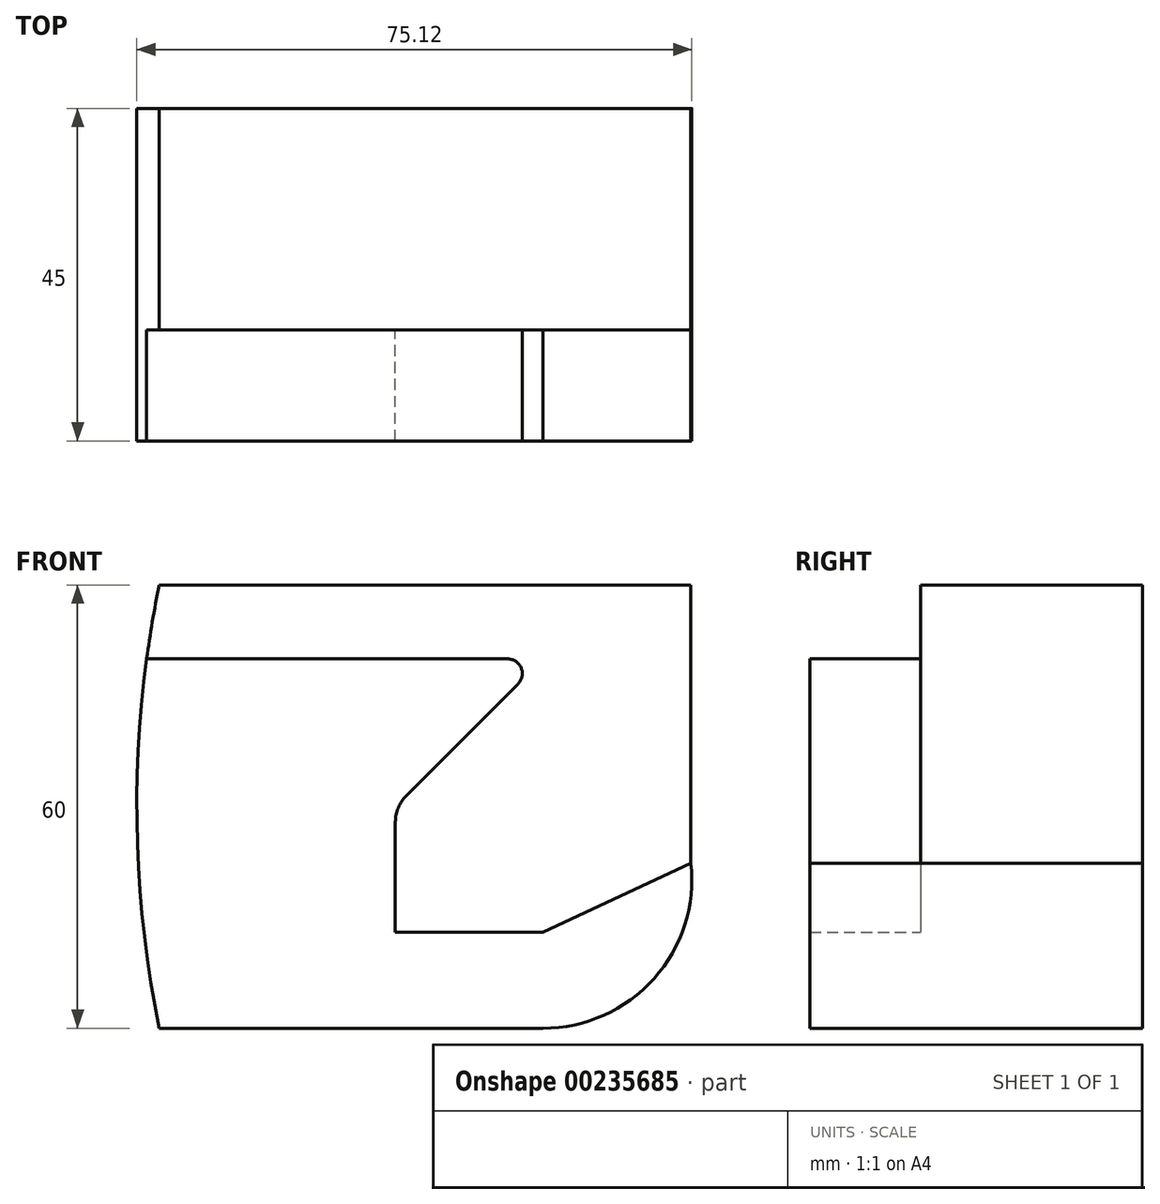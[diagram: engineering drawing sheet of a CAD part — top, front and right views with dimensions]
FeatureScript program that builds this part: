
annotation { "Feature Type Name" : "Feature", "Feature Type Description" : "" }
export const myFeature = defineFeature(function(context is Context, id is Id, definition is map)
    precondition{}
    {
        {
            var Q0;
            Q0=qCreatedBy(makeId("Front.planeOp"),FACE);
            var sketch = newSketch(context, id + "F0", { "sketchPlane" : qUnion([Q0])});
            skLineSegment(sketch, "E0", {"start": v(0, 0) * mm, "end": v(-51.97, 0) * mm});
            skLineSegment(sketch, "E1", {"start": v(-51.97, 60) * mm, "end": v(0, 60) * mm});
            skLineSegment(sketch, "E2", {"start": v(0, 60) * mm, "end": v(0, 50) * mm});
            skLineSegment(sketch, "E3", {"start": v(0, 50) * mm, "end": v(-18.54, 31.46) * mm});
            skLineSegment(sketch, "E4", {"start": v(-20, 27.93) * mm, "end": v(-20, 13) * mm});
            skLineSegment(sketch, "E5", {"start": v(-20, 13) * mm, "end": v(0, 13) * mm});
            skLineSegment(sketch, "E6", {"start": v(0, 13) * mm, "end": v(0, 0) * mm, "construction": true});
            skPoint(sketch, "E7.visualSharp", {"position": v(-20, 30) * mm});
            skArc(sketch, "E7.filletArc", {"start": v(-18.54, 31.46) * mm, "mid": v(-19.62, 29.84) * mm, "end": v(-20, 27.93) * mm});
            skArc(sketch, "E8", {"start": v(-51.97, 60) * mm, "mid": v(-55, 30) * mm, "end": v(-51.97, 0) * mm});
            skLineSegment(sketch, "E9", {"start": v(-51.97, 60) * mm, "end": v(-51.97, 0) * mm, "construction": true});
            skPoint(sketch, "E10", {"position": v(-51.97, 0) * mm});
            skArc(sketch, "E11", {"start": v(0, 0) * mm, "mid": v(14.99, 6.7) * mm, "end": v(20, 22.33) * mm});
            skLineSegment(sketch, "E12", {"start": v(20, 22.33) * mm, "end": v(0, 13) * mm});
            skSolve(sketch);
        }
        {
            var Q0;
            Q0 = qSketchRegion(id + "F0", true);
            extrude(context, id + "F1", {"entities" : qUnion([Q0]), "depth" : 30 * mm});
        }
        {
            var Q0;
            Q0=makeQuery(id+"F1.opExtrude","CAP_FACE",FACE,{"disambiguationData":[OSD([sQuery(id+"F0.wireOp",EDGE,"E0"),sQuery(id+"F0.wireOp",EDGE,"E1"),sQuery(id+"F0.wireOp",EDGE,"E2"),sQuery(id+"F0.wireOp",EDGE,"E3"),sQuery(id+"F0.wireOp",EDGE,"E4"),sQuery(id+"F0.wireOp",EDGE,"E5"),sQuery(id+"F0.wireOp",EDGE,"E7.filletArc"),sQuery(id+"F0.wireOp",EDGE,"E8"),sQuery(id+"F0.wireOp",EDGE,"E11"),sQuery(id+"F0.wireOp",EDGE,"E12")])],"isStart":true});
            var sketch = newSketch(context, id + "F2", { "sketchPlane" : qUnion([Q0])});
            skLineSegment(sketch, "E13.0", {"start": v(0, 60) * mm, "end": v(0, 50) * mm});
            skLineSegment(sketch, "E13.1", {"start": v(0, 50) * mm, "end": v(18.54, 31.46) * mm});
            skArc(sketch, "E13.2", {"start": v(18.54, 31.46) * mm, "mid": v(19.62, 29.84) * mm, "end": v(20, 27.93) * mm});
            skLineSegment(sketch, "E13.3", {"start": v(20, 27.93) * mm, "end": v(20, 13) * mm});
            skLineSegment(sketch, "E13.4", {"start": v(20, 13) * mm, "end": v(0, 13) * mm});
            skLineSegment(sketch, "E13.5", {"start": v(-20, 22.33) * mm, "end": v(0, 13) * mm});
            skLineSegment(sketch, "E14", {"start": v(0, 60) * mm, "end": v(-20, 60) * mm});
            skLineSegment(sketch, "E15", {"start": v(-20, 60) * mm, "end": v(-20, 22.33) * mm});
            skSolve(sketch);
        }
        {
            var Q0;
            Q0 = qSketchRegion(id + "F2", true);
            extrude(context, id + "F3", {"entities" : qUnion([Q0]), "operationType" : NewBodyOperationType.ADD, "oppositeDirection" : true, "depth" : 30 * mm});
        }
        {
            var Q0;
            Q0=makeQuery(id+"F3.boolean.opBoolean","MERGE",FACE,{"derivedFrom":[makeQuery(id+"F1.opExtrude","CAP_FACE",FACE,{"disambiguationData":[OSD([sQuery(id+"F0.wireOp",EDGE,"E0"),sQuery(id+"F0.wireOp",EDGE,"E1"),sQuery(id+"F0.wireOp",EDGE,"E2"),sQuery(id+"F0.wireOp",EDGE,"E3"),sQuery(id+"F0.wireOp",EDGE,"E4"),sQuery(id+"F0.wireOp",EDGE,"E5"),sQuery(id+"F0.wireOp",EDGE,"E7.filletArc"),sQuery(id+"F0.wireOp",EDGE,"E8"),sQuery(id+"F0.wireOp",EDGE,"E11"),sQuery(id+"F0.wireOp",EDGE,"E12")])],"isStart":false}),makeQuery(id+"F3.opExtrude","CAP_FACE",FACE,{"disambiguationData":[OSD([sQuery(id+"F2.wireOp",EDGE,"E13.0"),sQuery(id+"F2.wireOp",EDGE,"E13.1"),sQuery(id+"F2.wireOp",EDGE,"E13.2"),sQuery(id+"F2.wireOp",EDGE,"E13.3"),sQuery(id+"F2.wireOp",EDGE,"E13.4"),sQuery(id+"F2.wireOp",EDGE,"E13.5"),sQuery(id+"F2.wireOp",EDGE,"E14"),sQuery(id+"F2.wireOp",EDGE,"E15")])],"isStart":false})]});
            var sketch = newSketch(context, id + "F4", { "sketchPlane" : qUnion([Q0])});
            skLineSegment(sketch, "E16.0", {"start": v(0, 0) * mm, "end": v(-51.97, 0) * mm});
            skLineSegment(sketch, "E16.3", {"start": v(0, 50) * mm, "end": v(-18.54, 31.46) * mm});
            skLineSegment(sketch, "E16.4", {"start": v(-20, 27.93) * mm, "end": v(-20, 13) * mm});
            skLineSegment(sketch, "E16.5", {"start": v(-20, 13) * mm, "end": v(0, 13) * mm});
            skLineSegment(sketch, "E16.6", {"start": v(0, 13) * mm, "end": v(0, 0) * mm});
            skPoint(sketch, "E16.7", {"position": v(-20, 30) * mm});
            skArc(sketch, "E16.8", {"start": v(-18.54, 31.46) * mm, "mid": v(-19.62, 29.84) * mm, "end": v(-20, 27.93) * mm});
            skArc(sketch, "E16.9", {"start": v(-53.66, 50) * mm, "mid": v(-54.91, 24.93) * mm, "end": v(-51.97, 0) * mm});
            skLineSegment(sketch, "E16.10", {"start": v(-51.97, 50) * mm, "end": v(-51.97, 0) * mm});
            skPoint(sketch, "E16.11", {"position": v(-51.97, 0) * mm});
            skArc(sketch, "E16.12", {"start": v(0, 0) * mm, "mid": v(14.99, 6.7) * mm, "end": v(20, 22.33) * mm});
            skLineSegment(sketch, "E16.13", {"start": v(20, 22.33) * mm, "end": v(0, 13) * mm});
            skPoint(sketch, "E16.2.start.orphan", {"position": v(0, 60) * mm});
            skLineSegment(sketch, "E17", {"start": v(0, 50) * mm, "end": v(-53.66, 50) * mm});
            skPoint(sketch, "E18.orphan", {"position": v(-51.97, 60) * mm});
            skSolve(sketch);
        }
        {
            var Q0;
            Q0 = qSketchRegion(id + "F4", true);
            extrude(context, id + "F5", {"entities" : qUnion([Q0]), "operationType" : NewBodyOperationType.ADD, "depth" : 15 * mm});
        }
        {
            var Q0;
            Q0=makeQuery(id+"F5.opExtrude","SWEPT_EDGE",EDGE,{"disambiguationData":[OSD([sQuery(id+"F4.wireOp",EDGE,"E16.3"),sQuery(id+"F4.wireOp",EDGE,"E17")])]});
            fillet(context, id + "F6", {"entities" : qUnion([Q0]), "radius" : 2 * mm, "tangentPropagation" : true, "allowEdgeOverflow" : false});
        }
    });
